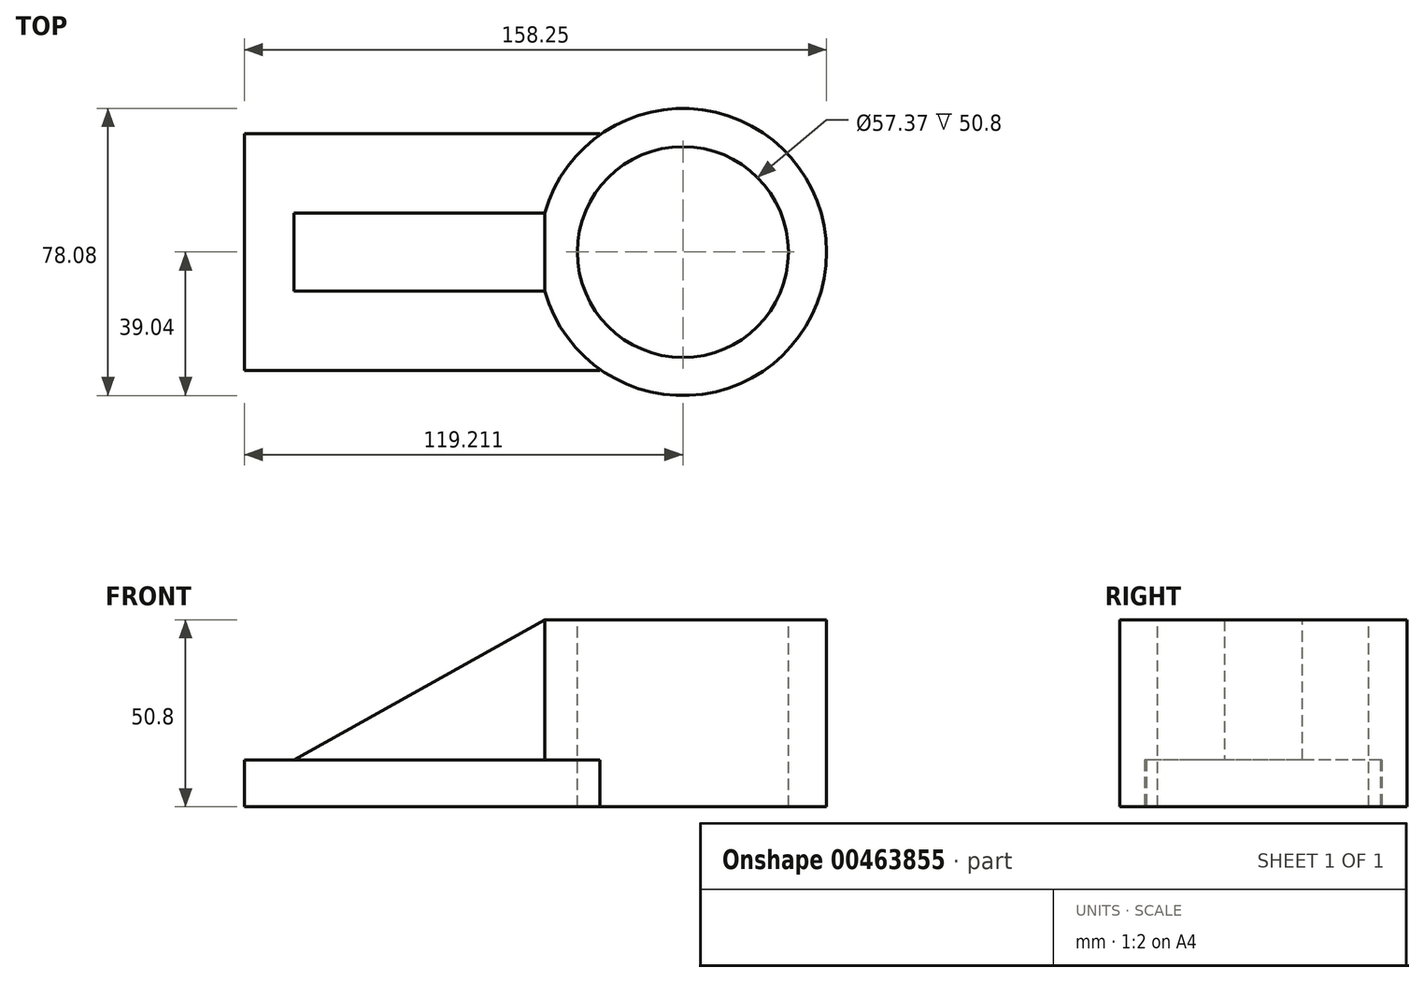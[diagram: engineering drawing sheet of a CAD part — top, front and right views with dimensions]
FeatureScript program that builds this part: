
annotation { "Feature Type Name" : "Feature", "Feature Type Description" : "" }
export const myFeature = defineFeature(function(context is Context, id is Id, definition is map)
    precondition{}
    {
        {
            var Q0;
            Q0=qCreatedBy(makeId("Top.planeOp"),FACE);
            var sketch = newSketch(context, id + "F0", { "sketchPlane" : qUnion([Q0])});
            skLineSegment(sketch, "E0.bottom", {"start": v(-48.31, 32.24) * mm, "end": v(48.31, 32.24) * mm});
            skLineSegment(sketch, "E0.top", {"start": v(-48.31, -32.24) * mm, "end": v(48.31, -32.24) * mm});
            skLineSegment(sketch, "E0.left", {"start": v(-48.31, 32.24) * mm, "end": v(-48.31, -32.24) * mm});
            skLineSegment(sketch, "E0.right", {"start": v(48.31, 32.24) * mm, "end": v(48.31, -32.24) * mm});
            skPoint(sketch, "E0.middle", {"position": v(0, 0) * mm});
            skSolve(sketch);
        }
        {
            var Q0;
            Q0=makeQuery(id+"F0.imprint","IMPRINT",FACE,{"disambiguationData":[TD([[makeQuery(id+"F0.imprint","IMPRINT",EDGE,{"derivedFrom":sQuery(id+"F0.wireOp",EDGE,"E0.bottom")}),-1.0]])]});
            extrude(context, id + "F1", {"entities" : qUnion([Q0]), "depth" : 12.7 * mm});
        }
        {
            var Q0;
            Q0=qCreatedBy(makeId("Top.planeOp"),FACE);
            var sketch = newSketch(context, id + "F2", { "sketchPlane" : qUnion([Q0])});
            skCircle(sketch, "E1", {"center": v(70.9, 0) * mm, "radius": 39.04 * mm});
            skSolve(sketch);
        }
        {
            var Q0;
            Q0=makeQuery(id+"F2.imprint","IMPRINT",FACE,{"disambiguationData":[TD([[makeQuery(id+"F2.imprint","IMPRINT",EDGE,{"derivedFrom":sQuery(id+"F2.wireOp",EDGE,"E1")}),1.0]])]});
            extrude(context, id + "F3", {"entities" : qUnion([Q0]), "operationType" : NewBodyOperationType.ADD, "depth" : 50.8 * mm});
        }
        {
            var Q0;
            Q0=makeQuery(id+"F3.opExtrude","CAP_FACE",FACE,{"disambiguationData":[OSD([sQuery(id+"F2.wireOp",EDGE,"E1")])],"isStart":false});
            var sketch = newSketch(context, id + "F4", { "sketchPlane" : qUnion([Q0])});
            skCircle(sketch, "E2", {"center": v(70.9, 0) * mm, "radius": 28.68 * mm});
            skSolve(sketch);
        }
        {
            var Q0;
            Q0=makeQuery(id+"F4.imprint","IMPRINT",FACE,{"disambiguationData":[TD([[makeQuery(id+"F4.imprint","IMPRINT",EDGE,{"derivedFrom":sQuery(id+"F4.wireOp",EDGE,"E2")}),1.0]])]});
            extrude(context, id + "F5", {"entities" : qUnion([Q0]), "operationType" : NewBodyOperationType.REMOVE, "oppositeDirection" : true, "depth" : 95 * mm});
        }
        {
            var Q0;
            Q0=makeQuery(id+"F1.opExtrude","CAP_FACE",FACE,{"disambiguationData":[OSD([sQuery(id+"F0.wireOp",EDGE,"E0.bottom"),sQuery(id+"F0.wireOp",EDGE,"E0.top"),sQuery(id+"F0.wireOp",EDGE,"E0.left"),sQuery(id+"F0.wireOp",EDGE,"E0.right")])],"isStart":false});
            var sketch = newSketch(context, id + "F6", { "sketchPlane" : qUnion([Q0])});
            skLineSegment(sketch, "E3.bottom", {"start": v(-34.82, 10.57) * mm, "end": v(34.82, 10.57) * mm});
            skLineSegment(sketch, "E3.top", {"start": v(-34.82, -10.57) * mm, "end": v(34.82, -10.57) * mm});
            skLineSegment(sketch, "E3.left", {"start": v(-34.82, 10.57) * mm, "end": v(-34.82, -10.57) * mm});
            skLineSegment(sketch, "E3.right", {"start": v(34.82, 10.57) * mm, "end": v(34.82, -10.57) * mm});
            skPoint(sketch, "E3.middle", {"position": v(0, 0) * mm});
            skSolve(sketch);
        }
        {
            var Q0;
            {var subQ0=sQuery(id+"F6.wireOp",EDGE,"E3.left");Q0=makeQuery(id+"F6.imprint","IMPRINT",FACE,{"disambiguationData":[TD([[makeQuery(id+"F6.imprint","IMPRINT",EDGE,{"derivedFrom":subQ0}),1.0]])]});}
            extrude(context, id + "F7", {"entities" : qUnion([Q0]), "operationType" : NewBodyOperationType.ADD, "depth" : 38.1 * mm});
        }
        {
            var Q0;
            Q0=makeQuery(id+"F7.opExtrude","SWEPT_FACE",FACE,{"disambiguationData":[OSD([sQuery(id+"F6.wireOp",EDGE,"E3.top")])]});
            var sketch = newSketch(context, id + "F8", { "sketchPlane" : qUnion([Q0])});
            skLineSegment(sketch, "E4", {"start": v(33.32, 50.8) * mm, "end": v(-34.82, 12.7) * mm});
            skSolve(sketch);
        }
        {
            var Q0;
            Q0=makeQuery(id+"F8.imprint","IMPRINT",FACE,{"disambiguationData":[TD([[makeQuery(id+"F8.imprint","IMPRINT",EDGE,{"derivedFrom":sQuery(id+"F8.wireOp",EDGE,"E4")}),-1.0]])]});
            extrude(context, id + "F9", {"entities" : qUnion([Q0]), "operationType" : NewBodyOperationType.REMOVE, "oppositeDirection" : true, "depth" : 72.9 * mm});
        }
    });
